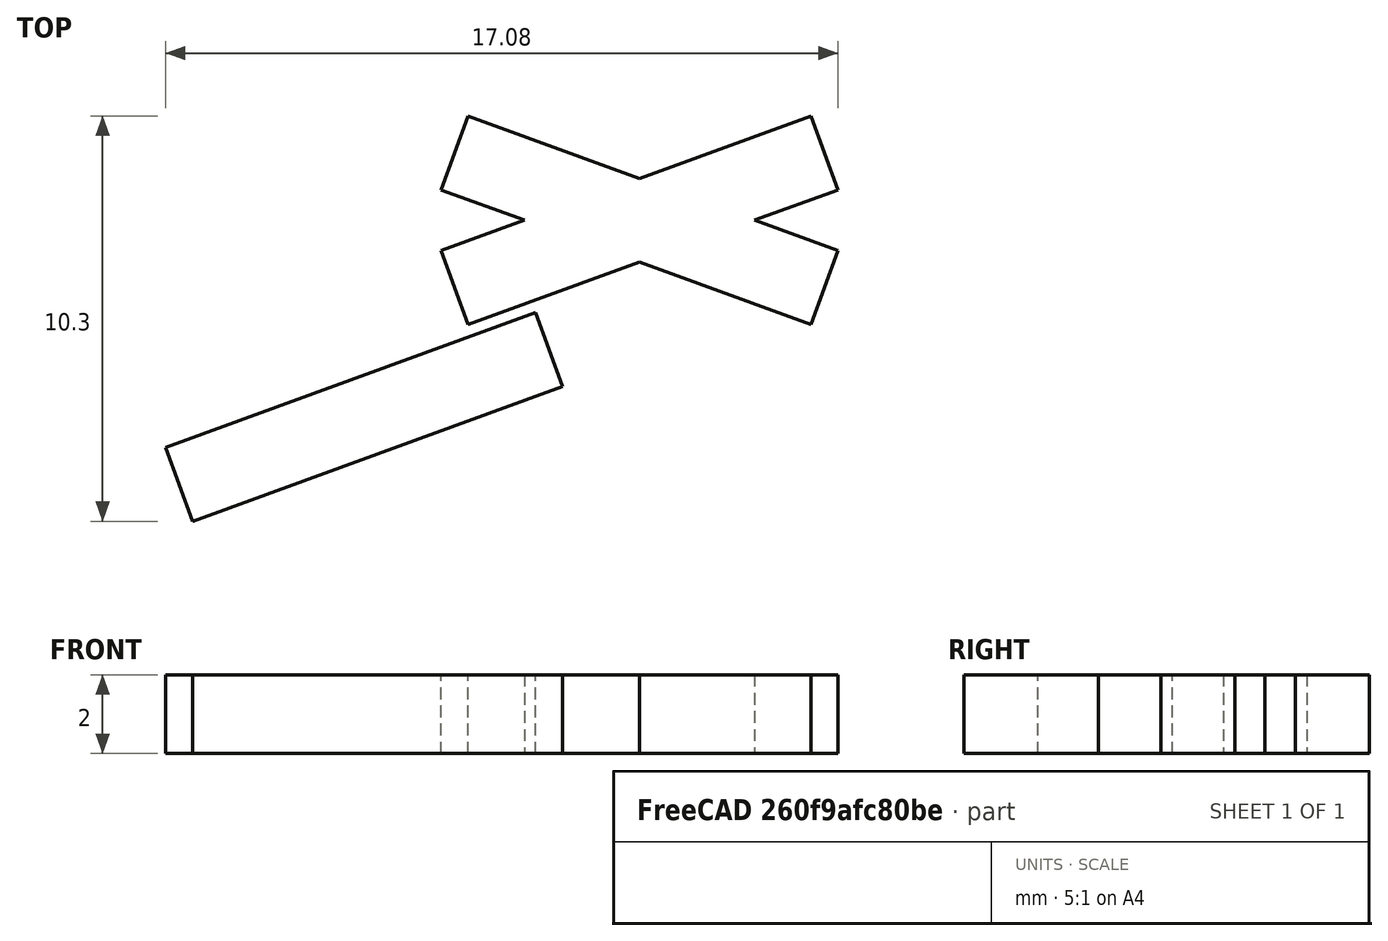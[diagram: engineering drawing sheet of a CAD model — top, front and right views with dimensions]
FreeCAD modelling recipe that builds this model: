
FCSTD DOCUMENT  (FreeCAD 1.0R39319 (Git))
Label: ojt1_t06_p01_rotacions
License: All rights reserved
LicenseURL: https://en.wikipedia.org/wiki/All_rights_reserved
objects: Part::Box×2, PartDesign::Boolean×1, PartDesign::Body×1
note: 5 computed .brp shape members not serialized (recipe doc carries the construction recipe); baked Part::Feature solids carry a one-line shape summary decoded from their .brp

FEATURE [Part::Box] Box  label="Cubo"
  AttacherType = Attacher::AttachEngine3D
  Height = 2
  Length = 10
  Placement = pos=(-5.04048,0.770408,0) rot=(0,0,4;5.93412rad)
  Width = 2
FEATURE [Part::Box] Box001  label="Cubo001"
  AttacherType = Attacher::AttachEngine3D
  Height = 2
  Length = 10
  Placement = pos=(-4.35644,-2.64979,0) rot=(0,0,4;0.349066rad)
  Width = 2
FEATURE [PartDesign::Boolean] Boolean
  Group = -> [Box,Box001]
  Refine = true
  Suppressed = false
  Type = 0
  UsePlacement = true
FEATURE [PartDesign::Body] Body
  AllowCompound = false
  Group = -> [Boolean]
  Origin = -> Origin
  Placement = pos=(7,5,0) rot=(0,0,1;0rad)
  Tip = -> Boolean
